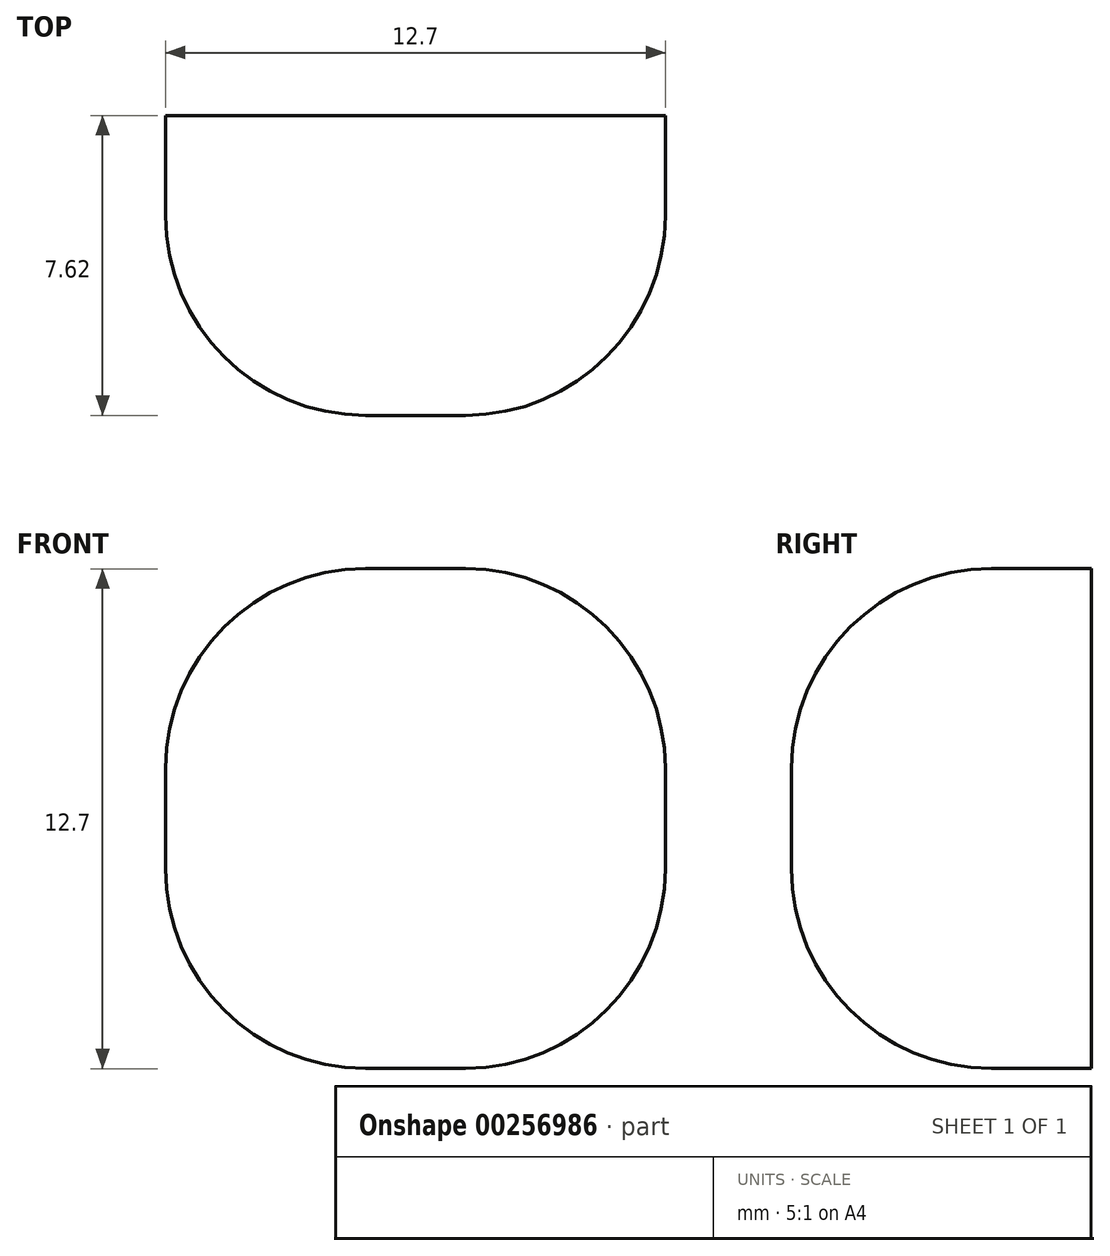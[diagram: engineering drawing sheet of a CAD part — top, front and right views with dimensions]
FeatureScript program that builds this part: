
annotation { "Feature Type Name" : "Feature", "Feature Type Description" : "" }
export const myFeature = defineFeature(function(context is Context, id is Id, definition is map)
    precondition{}
    {
        {
            var Q0;
            Q0=qCreatedBy(makeId("Front.planeOp"),FACE);
            var sketch = newSketch(context, id + "F0", { "sketchPlane" : qUnion([Q0])});
            skLineSegment(sketch, "E0.bottom", {"start": v(-7.63, 3.24) * mm, "end": v(5.07, 3.24) * mm});
            skLineSegment(sketch, "E0.top", {"start": v(-7.63, -9.46) * mm, "end": v(5.07, -9.46) * mm});
            skLineSegment(sketch, "E0.left", {"start": v(-7.63, 3.24) * mm, "end": v(-7.63, -9.46) * mm});
            skLineSegment(sketch, "E0.right", {"start": v(5.07, 3.24) * mm, "end": v(5.07, -9.46) * mm});
            skSolve(sketch);
        }
        {
            var Q0;
            Q0=makeQuery(id+"F0.imprint","IMPRINT",FACE,{"disambiguationData":[TD([[makeQuery(id+"F0.imprint","IMPRINT",EDGE,{"derivedFrom":sQuery(id+"F0.wireOp",EDGE,"E0.bottom")}),-1.0]])]});
            extrude(context, id + "F1", {"entities" : qUnion([Q0]), "depth" : 7.62 * mm});
        }
        {
            var Q0;
            Q0=makeQuery(id+"F1.opExtrude","CAP_EDGE",EDGE,{"disambiguationData":[OSD([sQuery(id+"F0.wireOp",EDGE,"E0.left")])],"isStart":false});
            var Q1;
            Q1=makeQuery(id+"F1.opExtrude","CAP_EDGE",EDGE,{"disambiguationData":[OSD([sQuery(id+"F0.wireOp",EDGE,"E0.bottom")])],"isStart":false});
            var Q2;
            Q2=makeQuery(id+"F1.opExtrude","CAP_EDGE",EDGE,{"disambiguationData":[OSD([sQuery(id+"F0.wireOp",EDGE,"E0.right")])],"isStart":false});
            var Q3;
            Q3=makeQuery(id+"F1.opExtrude","CAP_EDGE",EDGE,{"disambiguationData":[OSD([sQuery(id+"F0.wireOp",EDGE,"E0.top")])],"isStart":false});
            var Q4;
            Q4=makeQuery(id+"F1.opExtrude","SWEPT_EDGE",EDGE,{"disambiguationData":[OSD([sQuery(id+"F0.wireOp",EDGE,"E0.bottom"),sQuery(id+"F0.wireOp",EDGE,"E0.left")])]});
            var Q5;
            Q5=makeQuery(id+"F1.opExtrude","SWEPT_EDGE",EDGE,{"disambiguationData":[OSD([sQuery(id+"F0.wireOp",EDGE,"E0.bottom"),sQuery(id+"F0.wireOp",EDGE,"E0.right")])]});
            var Q6;
            Q6=makeQuery(id+"F1.opExtrude","SWEPT_EDGE",EDGE,{"disambiguationData":[OSD([sQuery(id+"F0.wireOp",EDGE,"E0.top"),sQuery(id+"F0.wireOp",EDGE,"E0.right")])]});
            var Q7;
            Q7=makeQuery(id+"F1.opExtrude","SWEPT_EDGE",EDGE,{"disambiguationData":[OSD([sQuery(id+"F0.wireOp",EDGE,"E0.top"),sQuery(id+"F0.wireOp",EDGE,"E0.left")])]});
            fillet(context, id + "F2", {"entities" : qUnion([Q0, Q1, Q2, Q3, Q4, Q5, Q6, Q7]), "radius" : 5.08 * mm, "tangentPropagation" : true, "allowEdgeOverflow" : false});
        }
    });
